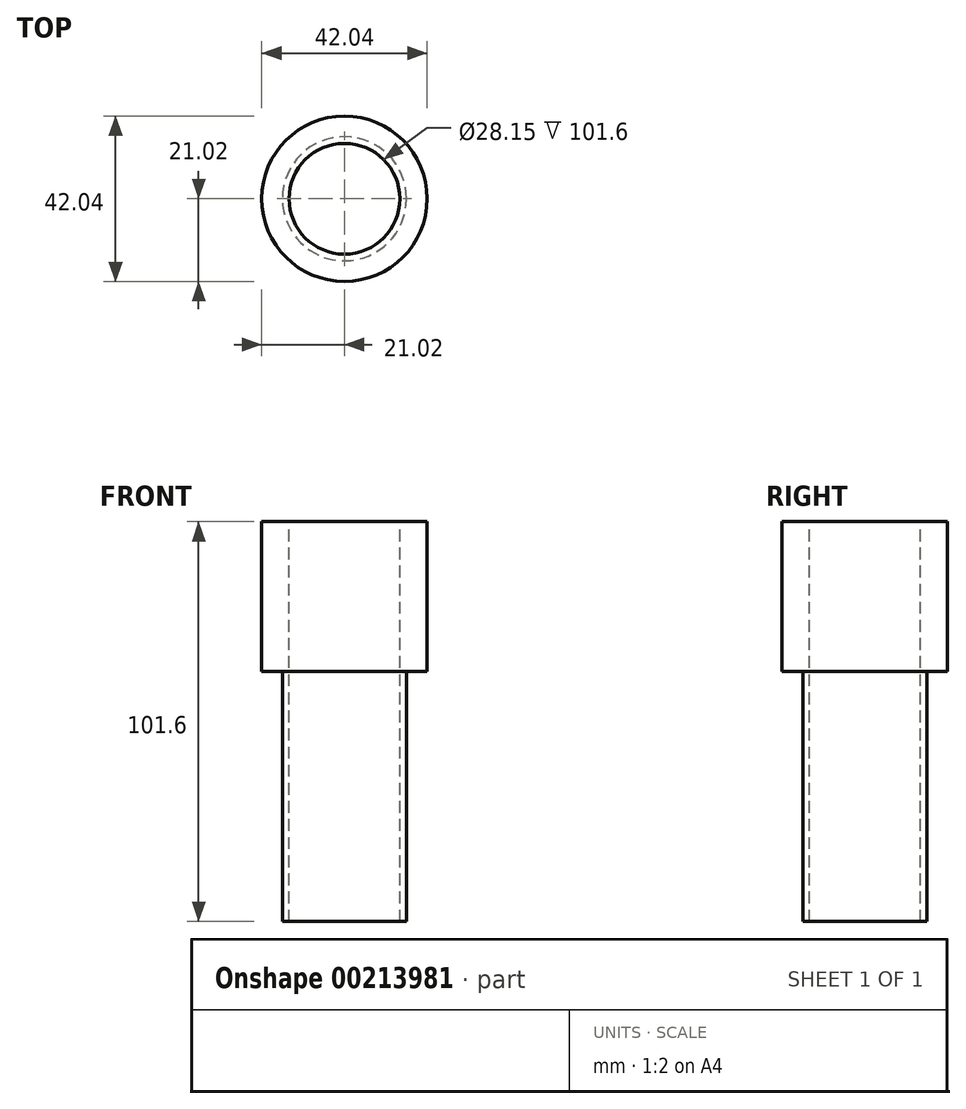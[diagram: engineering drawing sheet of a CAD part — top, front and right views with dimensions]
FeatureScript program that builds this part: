
annotation { "Feature Type Name" : "Feature", "Feature Type Description" : "" }
export const myFeature = defineFeature(function(context is Context, id is Id, definition is map)
    precondition{}
    {
        {
            var Q0;
            Q0=qCreatedBy(makeId("Top.planeOp"),FACE);
            var sketch = newSketch(context, id + "F0", { "sketchPlane" : qUnion([Q0])});
            skCircle(sketch, "E0", {"center": v(0, 0) * mm, "radius": 15.76 * mm});
            skSolve(sketch);
        }
        {
            var Q0;
            Q0=qSketchRegion(id+"F0",true);
            extrude(context, id + "F1", {"entities" : qUnion([Q0]), "oppositeDirection" : true, "depth" : 101.6 * mm});
        }
        {
            var Q0;
            Q0=qCreatedBy(makeId("Top.planeOp"),FACE);
            var sketch = newSketch(context, id + "F2", { "sketchPlane" : qUnion([Q0])});
            skCircle(sketch, "E1", {"center": v(0, 0) * mm, "radius": 21.02 * mm});
            skSolve(sketch);
        }
        {
            var Q0;
            Q0=qSketchRegion(id+"F2",true);
            extrude(context, id + "F3", {"entities" : qUnion([Q0]), "operationType" : NewBodyOperationType.ADD, "oppositeDirection" : true, "depth" : 38.1 * mm});
        }
        {
            var Q0;
            Q0=makeQuery(id+"F3.boolean.opBoolean","MERGE",FACE,{"derivedFrom":[makeQuery(id+"F1.opExtrude","CAP_FACE",FACE,{"disambiguationData":[OSD([sQuery(id+"F0.wireOp",EDGE,"E0")])],"isStart":true}),makeQuery(id+"F3.opExtrude","CAP_FACE",FACE,{"disambiguationData":[OSD([sQuery(id+"F2.wireOp",EDGE,"E1")])],"isStart":true})]});
            var sketch = newSketch(context, id + "F4", { "sketchPlane" : qUnion([Q0])});
            skCircle(sketch, "E2", {"center": v(0, 0) * mm, "radius": 14.07 * mm});
            skSolve(sketch);
        }
        {
            var Q0;
            Q0=qSketchRegion(id+"F4",true);
            extrude(context, id + "F5", {"entities" : qUnion([Q0]), "operationType" : NewBodyOperationType.REMOVE, "endBound" : BoundingType.THROUGH_ALL, "oppositeDirection" : true, "depth" : 25.4 * mm});
        }
    });
